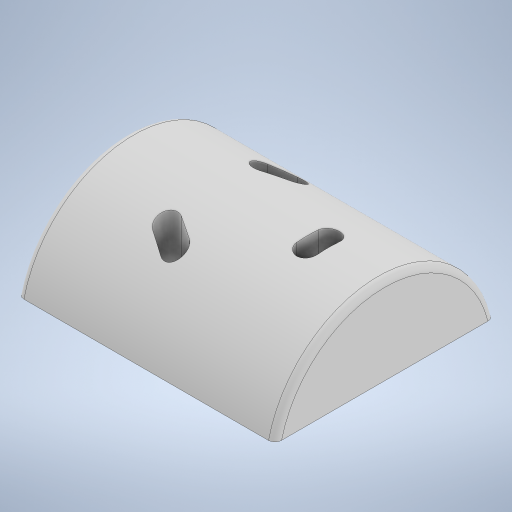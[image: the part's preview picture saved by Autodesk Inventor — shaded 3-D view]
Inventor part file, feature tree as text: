
AUTODESK INVENTOR PART (.ipt)
format: ipt  version: 2024.2 (Build 282272000, 272)  size: 313,856 bytes
history: native  units: mm
features: extrude x3, other x1, sketch x1, revolve x1, fillet x1
ambient origin geometry x8: Origin, YZ Plane, XZ Plane, XY Plane, X Axis, Y Axis, Z Axis, Center Point
bodies: Body1 (feature_tree)
feature tree (7):
  other  "Bryła1"
  sketch  "Szkic1"
  revolve  "Obrót2"
  extrude  "Wyciągnięcie proste1"  Depth=39.24mm
  extrude  "Wyciągnięcie proste2"  Depth=3.5mm
  extrude  "Wyciągnięcie proste3"  Depth=3.490659mm
  fillet  "Zaokrąglenie1"  Radius=30.0mm
